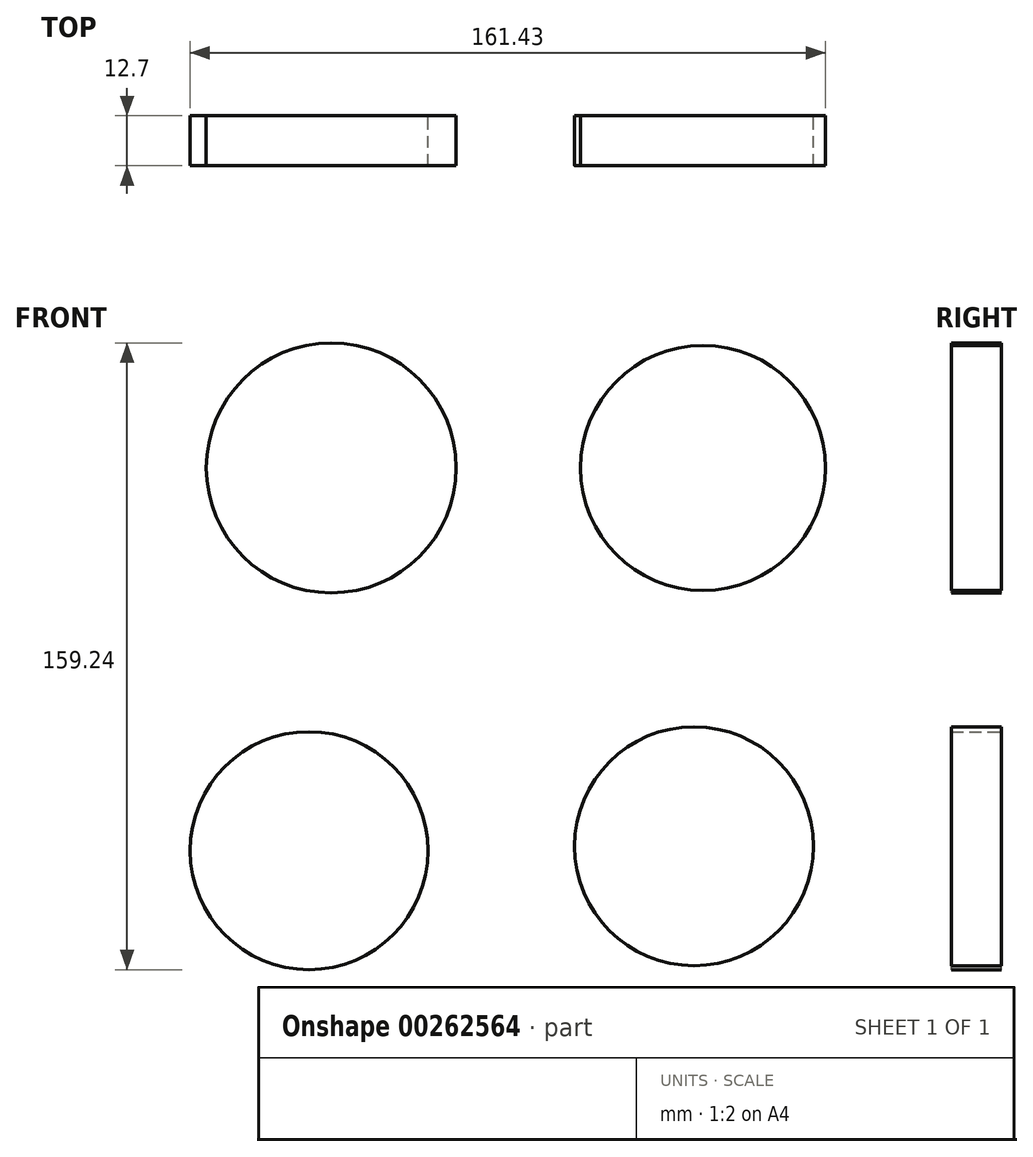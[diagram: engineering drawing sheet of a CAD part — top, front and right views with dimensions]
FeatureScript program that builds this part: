
annotation { "Feature Type Name" : "Feature", "Feature Type Description" : "" }
export const myFeature = defineFeature(function(context is Context, id is Id, definition is map)
    precondition{}
    {
        {
            var Q0;
            Q0=qCreatedBy(makeId("Front.planeOp"),FACE);
            var sketch = newSketch(context, id + "F0", { "sketchPlane" : qUnion([Q0])});
            skCircle(sketch, "E0", {"center": v(-45.4, 47.42) * mm, "radius": 31.75 * mm});
            skCircle(sketch, "E1", {"center": v(49.03, 47.42) * mm, "radius": 31.12 * mm});
            skCircle(sketch, "E2", {"center": v(-51.05, -49.84) * mm, "radius": 30.23 * mm});
            skCircle(sketch, "E3", {"center": v(46.77, -48.71) * mm, "radius": 30.35 * mm});
            skSolve(sketch);
        }
        {
            var Q0;
            Q0=makeQuery(id+"F0.imprint","IMPRINT",FACE,{"disambiguationData":[TD([[makeQuery(id+"F0.imprint","IMPRINT",EDGE,{"derivedFrom":sQuery(id+"F0.wireOp",EDGE,"E2")}),1.0]])]});
            var Q1;
            Q1=makeQuery(id+"F0.imprint","IMPRINT",FACE,{"disambiguationData":[TD([[makeQuery(id+"F0.imprint","IMPRINT",EDGE,{"derivedFrom":sQuery(id+"F0.wireOp",EDGE,"E3")}),1.0]])]});
            var Q2;
            Q2=makeQuery(id+"F0.imprint","IMPRINT",FACE,{"disambiguationData":[TD([[makeQuery(id+"F0.imprint","IMPRINT",EDGE,{"derivedFrom":sQuery(id+"F0.wireOp",EDGE,"E1")}),1.0]])]});
            var Q3;
            Q3=makeQuery(id+"F0.imprint","IMPRINT",FACE,{"disambiguationData":[TD([[makeQuery(id+"F0.imprint","IMPRINT",EDGE,{"derivedFrom":sQuery(id+"F0.wireOp",EDGE,"E0")}),1.0]])]});
            extrude(context, id + "F1", {"entities" : qUnion([Q0, Q1, Q2, Q3]), "depth" : 12.7 * mm});
        }
    });
